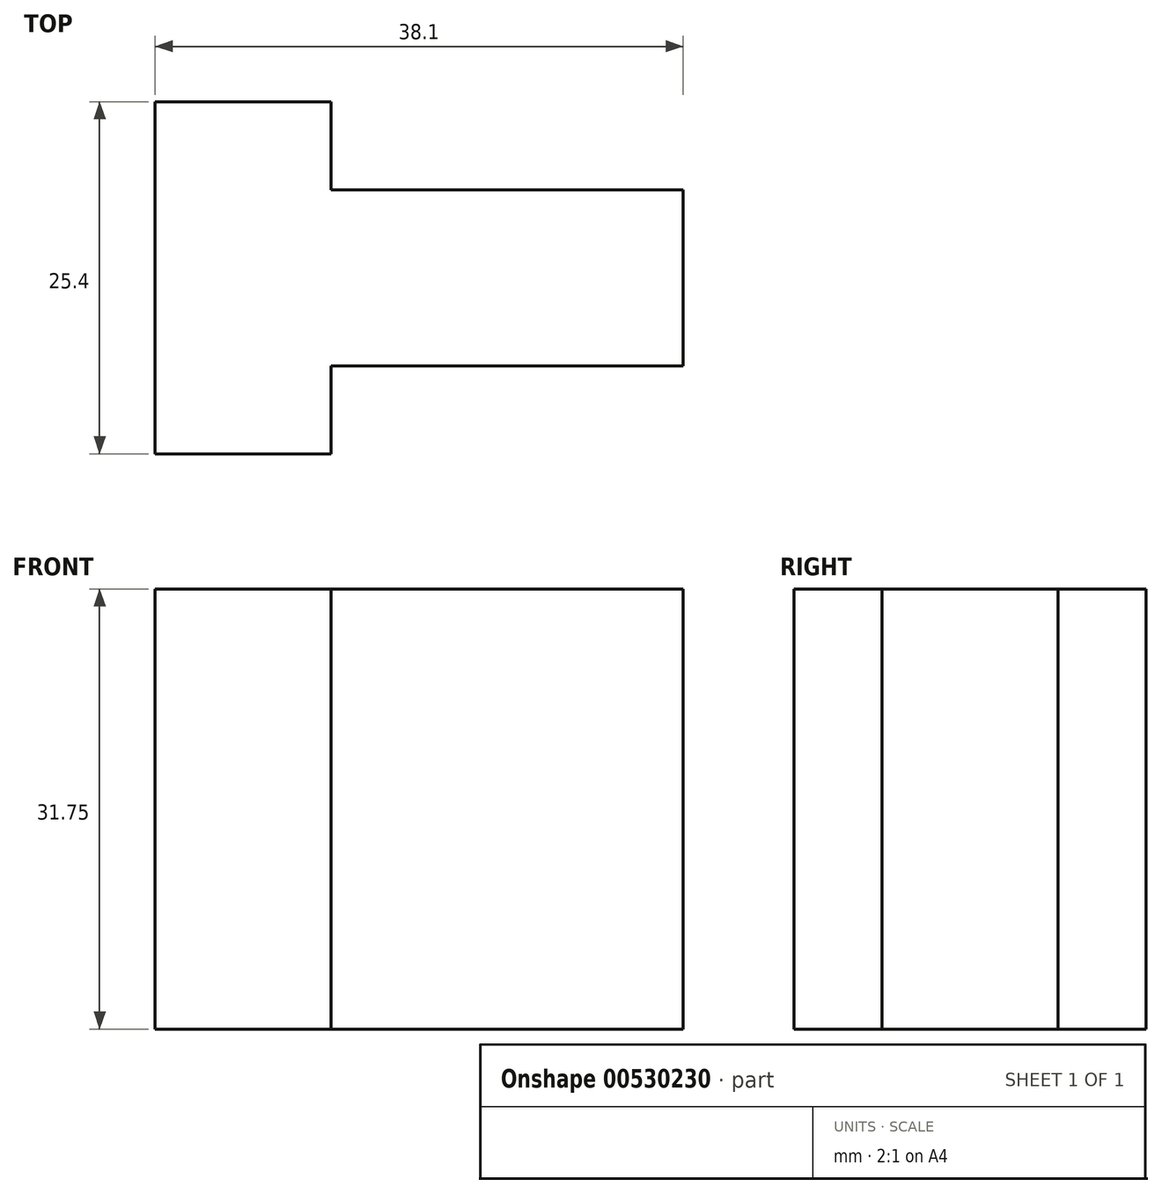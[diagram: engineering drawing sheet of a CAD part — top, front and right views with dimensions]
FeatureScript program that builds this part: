
annotation { "Feature Type Name" : "Feature", "Feature Type Description" : "" }
export const myFeature = defineFeature(function(context is Context, id is Id, definition is map)
    precondition{}
    {
        {
            var Q0;
            Q0=qCreatedBy(makeId("Front.planeOp"),FACE);
            var sketch = newSketch(context, id + "F0", { "sketchPlane" : qUnion([Q0])});
            skLineSegment(sketch, "E0", {"start": v(-68.97, 0) * mm, "end": v(-30.87, 0) * mm});
            skLineSegment(sketch, "E1", {"start": v(-30.87, 0) * mm, "end": v(-30.87, 31.75) * mm});
            skLineSegment(sketch, "E2", {"start": v(-30.87, 31.75) * mm, "end": v(-68.97, 31.75) * mm});
            skLineSegment(sketch, "E3", {"start": v(-68.97, 31.75) * mm, "end": v(-68.97, 0) * mm});
            skSolve(sketch);
        }
        {
            var Q0;
            Q0=makeQuery(id+"F0.imprint","IMPRINT",FACE,{"disambiguationData":[TD([[makeQuery(id+"F0.imprint","IMPRINT",EDGE,{"derivedFrom":sQuery(id+"F0.wireOp",EDGE,"E0")}),1.0]])]});
            var sketch = newSketch(context, id + "F1", { "sketchPlane" : qUnion([Q0])});
            skSolve(sketch);
        }
        {
            var Q0;
            Q0 = qSketchRegion(id + "F1", true);
            var Q1;
            Q1=makeQuery(id+"F0.imprint","IMPRINT",FACE,{"disambiguationData":[TD([[makeQuery(id+"F0.imprint","IMPRINT",EDGE,{"derivedFrom":sQuery(id+"F0.wireOp",EDGE,"E0")}),1.0]])]});
            extrude(context, id + "F2", {"entities" : qUnion([Q0, Q1]), "depth" : 25.4 * mm, "offsetDistance" : 25.4 * mm});
        }
        {
            var Q0;
            Q0=makeQuery(id+"F2.opExtrude","SWEPT_FACE",FACE,{"disambiguationData":[OSD([sQuery(id+"F0.wireOp",EDGE,"E0")])]});
            var sketch = newSketch(context, id + "F3", { "sketchPlane" : qUnion([Q0])});
            skLineSegment(sketch, "E4", {"start": v(-56.27, 0) * mm, "end": v(-56.27, 6.35) * mm});
            skLineSegment(sketch, "E5", {"start": v(-56.27, 6.35) * mm, "end": v(-30.87, 6.35) * mm});
            skLineSegment(sketch, "E6", {"start": v(-30.87, 6.35) * mm, "end": v(-30.87, 0) * mm});
            skLineSegment(sketch, "E7", {"start": v(-30.87, 0) * mm, "end": v(-56.27, 0) * mm});
            skSolve(sketch);
        }
        {
            var Q0;
            Q0=makeQuery(id+"F3.imprint","IMPRINT",FACE,{"disambiguationData":[TD([[makeQuery(id+"F3.imprint","IMPRINT",EDGE,{"derivedFrom":sQuery(id+"F3.wireOp",EDGE,"E4")}),-1.0]])]});
            extrude(context, id + "F4", {"entities" : qUnion([Q0]), "operationType" : NewBodyOperationType.REMOVE, "oppositeDirection" : true, "depth" : 25.4 * mm, "offsetDistance" : 25.4 * mm});
        }
        {
            var Q0;
            Q0=makeQuery(id+"F4.boolean.opBoolean","COPY",FACE,{"derivedFrom":makeQuery(id+"F4.opExtrude","CAP_FACE",FACE,{"disambiguationData":[OSD([sQuery(id+"F3.wireOp",EDGE,"E4"),sQuery(id+"F3.wireOp",EDGE,"E5"),sQuery(id+"F3.wireOp",EDGE,"E6"),sQuery(id+"F3.wireOp",EDGE,"E7")])],"isStart":false})});
            extrude(context, id + "F5", {"entities" : qUnion([Q0]), "operationType" : NewBodyOperationType.REMOVE, "oppositeDirection" : true, "depth" : 25.4 * mm, "offsetDistance" : 25.4 * mm});
        }
        {
            var Q0;
            Q0=makeQuery(id+"F2.opExtrude","SWEPT_FACE",FACE,{"disambiguationData":[OSD([sQuery(id+"F0.wireOp",EDGE,"E0")])]});
            var sketch = newSketch(context, id + "F6", { "sketchPlane" : qUnion([Q0])});
            skLineSegment(sketch, "E8", {"start": v(-56.27, 25.4) * mm, "end": v(-56.27, 19.05) * mm});
            skLineSegment(sketch, "E9", {"start": v(-56.27, 19.05) * mm, "end": v(-30.87, 19.05) * mm});
            skSolve(sketch);
        }
        {
            var Q0;
            {var subQ0=sQuery(id+"F6.wireOp",EDGE,"E8");Q0=makeQuery(id+"F6.imprint","IMPRINT",FACE,{"disambiguationData":[TD([[makeQuery(id+"F6.imprint","IMPRINT",EDGE,{"derivedFrom":subQ0}),1.0]])]});}
            extrude(context, id + "F7", {"entities" : qUnion([Q0]), "operationType" : NewBodyOperationType.REMOVE, "oppositeDirection" : true, "depth" : 50.8 * mm, "offsetDistance" : 25.4 * mm});
        }
    });
